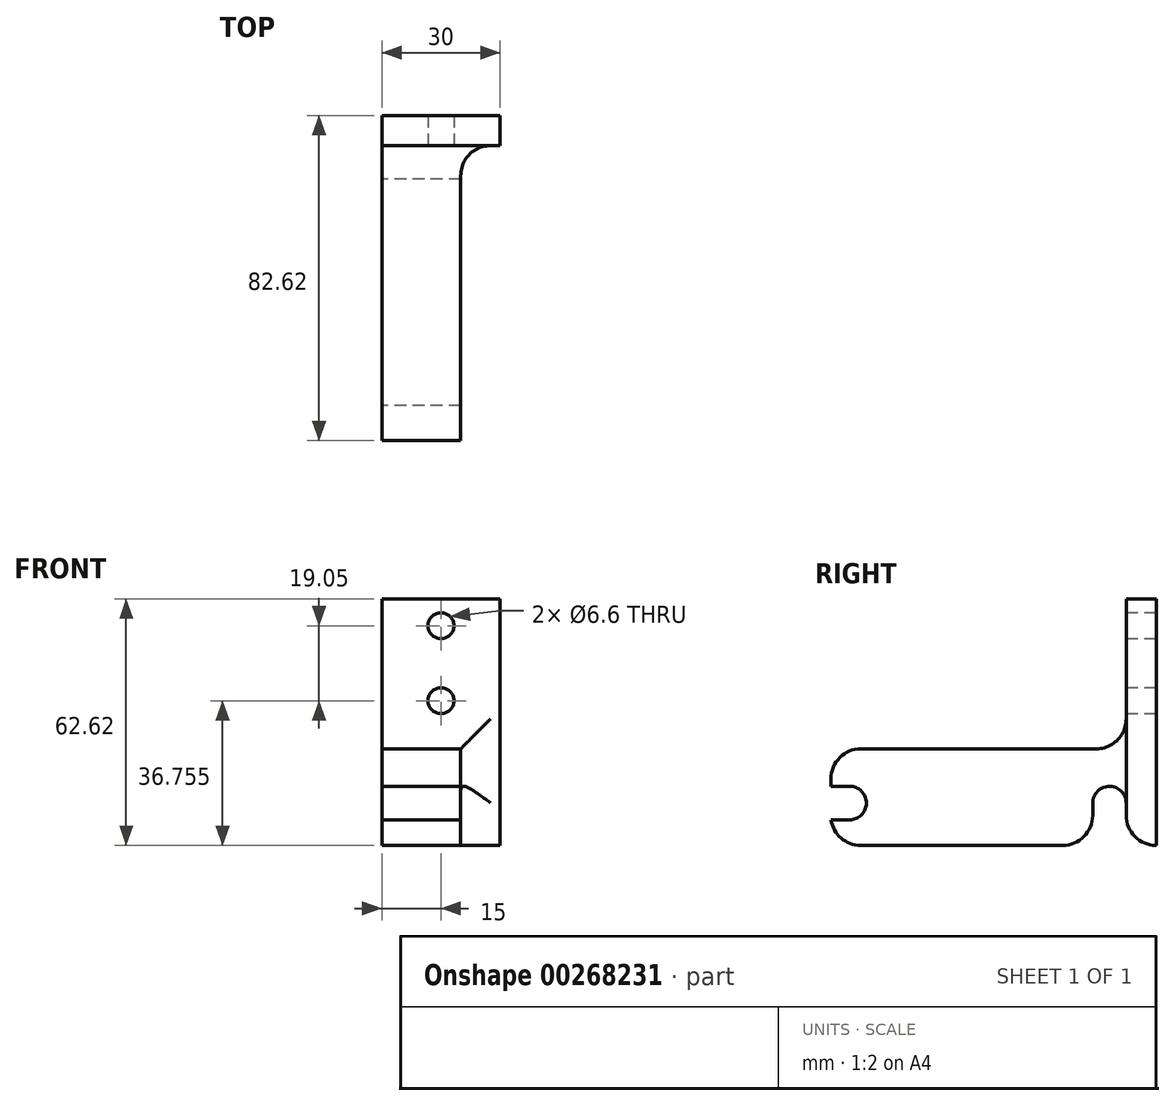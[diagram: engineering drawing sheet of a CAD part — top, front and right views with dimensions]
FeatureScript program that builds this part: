
annotation { "Feature Type Name" : "Feature", "Feature Type Description" : "" }
export const myFeature = defineFeature(function(context is Context, id is Id, definition is map)
    precondition{}
    {
        {
            var Q0;
            Q0=qCreatedBy(makeId("Right.planeOp"),FACE);
            var sketch = newSketch(context, id + "F0", { "sketchPlane" : qUnion([Q0])});
            skLineSegment(sketch, "E0", {"start": v(0, 0) * mm, "end": v(0, 6.5) * mm});
            skLineSegment(sketch, "E1", {"start": v(0, 6.5) * mm, "end": v(4.75, 6.5) * mm});
            skLineSegment(sketch, "E2", {"start": v(4.75, 15) * mm, "end": v(0, 15) * mm});
            skLineSegment(sketch, "E3", {"start": v(0, 15) * mm, "end": v(0, 16.9) * mm});
            skLineSegment(sketch, "E4", {"start": v(7.62, 24.53) * mm, "end": v(75, 24.53) * mm});
            skLineSegment(sketch, "E5", {"start": v(75, 24.53) * mm, "end": v(75, 62.63) * mm});
            skLineSegment(sketch, "E6", {"start": v(75, 62.63) * mm, "end": v(82.62, 62.63) * mm});
            skLineSegment(sketch, "E7", {"start": v(82.62, 62.63) * mm, "end": v(82.62, 0) * mm});
            skLineSegment(sketch, "E8", {"start": v(82.62, 0) * mm, "end": v(75, 0) * mm});
            skLineSegment(sketch, "E9", {"start": v(75, 0) * mm, "end": v(75, 10.75) * mm});
            skLineSegment(sketch, "E10", {"start": v(66.5, 10.75) * mm, "end": v(66.5, 0) * mm});
            skArc(sketch, "E11", {"start": v(4.75, 6.5) * mm, "mid": v(9, 10.75) * mm, "end": v(4.75, 15) * mm});
            skPoint(sketch, "E11.first.point", {"position": v(9, 10.75) * mm});
            skPoint(sketch, "E11.second.point", {"position": v(4.75, 15) * mm});
            skPoint(sketch, "E11.third.point", {"position": v(4.75, 6.5) * mm});
            skArc(sketch, "E12", {"start": v(75, 10.75) * mm, "mid": v(70.75, 15) * mm, "end": v(66.5, 10.75) * mm});
            skPoint(sketch, "E12.first.point", {"position": v(70.75, 15) * mm});
            skPoint(sketch, "E12.second.point", {"position": v(66.5, 10.75) * mm});
            skPoint(sketch, "E12.third.point", {"position": v(75, 10.75) * mm});
            skPoint(sketch, "E13.orphan", {"position": v(9, 15) * mm});
            skPoint(sketch, "E14.orphan", {"position": v(9, 6.5) * mm});
            skPoint(sketch, "E15.orphan", {"position": v(66.5, 15) * mm});
            skPoint(sketch, "E16.orphan", {"position": v(75, 15) * mm});
            skLineSegment(sketch, "E17", {"start": v(0, 0) * mm, "end": v(66.5, 0) * mm});
            skPoint(sketch, "E18.visualSharp", {"position": v(0, 24.53) * mm});
            skArc(sketch, "E18.filletArc", {"start": v(7.62, 24.53) * mm, "mid": v(2.23, 22.3) * mm, "end": v(0, 16.9) * mm});
            skSolve(sketch);
        }
        {
            var Q0;
            Q0=makeQuery(id+"F0.imprint","IMPRINT",FACE,{"disambiguationData":[TD([[makeQuery(id+"F0.imprint","IMPRINT",EDGE,{"derivedFrom":sQuery(id+"F0.wireOp",EDGE,"E0")}),-1.0]])]});
            extrude(context, id + "F1", {"entities" : qUnion([Q0]), "depth" : 30 * mm});
        }
        {
            var Q0;
            Q0=makeQuery(id+"F1.opExtrude","SWEPT_FACE",FACE,{"disambiguationData":[OSD([sQuery(id+"F0.wireOp",EDGE,"E4")])]});
            var sketch = newSketch(context, id + "F2", { "sketchPlane" : qUnion([Q0])});
            skLineSegment(sketch, "E19.bottom", {"start": v(30, 75) * mm, "end": v(20, 75) * mm});
            skLineSegment(sketch, "E19.top", {"start": v(30, 0) * mm, "end": v(20, 0) * mm});
            skLineSegment(sketch, "E19.left", {"start": v(30, 75) * mm, "end": v(30, 0) * mm});
            skLineSegment(sketch, "E19.right", {"start": v(20, 75) * mm, "end": v(20, 0) * mm});
            skPoint(sketch, "E20.0", {"position": v(30, 0) * mm});
            skSolve(sketch);
        }
        {
            var Q0;
            Q0=makeQuery(id+"F2.imprint","IMPRINT",FACE,{"disambiguationData":[TD([[makeQuery(id+"F2.imprint","IMPRINT",EDGE,{"derivedFrom":sQuery(id+"F2.wireOp",EDGE,"E19.bottom")}),1.0]])]});
            var Q1;
            {var subQ0=sQuery(id+"F2.wireOp",EDGE,"E19.top");Q1=makeQuery(id+"F2.imprint","IMPRINT",FACE,{"disambiguationData":[TD([[makeQuery(id+"F2.imprint","IMPRINT",EDGE,{"derivedFrom":subQ0}),-1.0]])]});}
            var Q2;
            Q2=makeQuery(id+"F1.opExtrude","SWEPT_BODY",BODY,{"disambiguationData":[OSD([sQuery(id+"F0.wireOp",EDGE,"E0"),sQuery(id+"F0.wireOp",EDGE,"E1"),sQuery(id+"F0.wireOp",EDGE,"E2"),sQuery(id+"F0.wireOp",EDGE,"E3"),sQuery(id+"F0.wireOp",EDGE,"E4"),sQuery(id+"F0.wireOp",EDGE,"E5"),sQuery(id+"F0.wireOp",EDGE,"E6"),sQuery(id+"F0.wireOp",EDGE,"E7"),sQuery(id+"F0.wireOp",EDGE,"E8"),sQuery(id+"F0.wireOp",EDGE,"E9"),sQuery(id+"F0.wireOp",EDGE,"E10"),sQuery(id+"F0.wireOp",EDGE,"E11"),sQuery(id+"F0.wireOp",EDGE,"E12"),sQuery(id+"F0.wireOp",EDGE,"E17")])]});
            extrude(context, id + "F3", {"entities" : qUnion([Q0, Q1]), "operationType" : NewBodyOperationType.REMOVE, "endBound" : BoundingType.UP_TO_BODY, "oppositeDirection" : true, "endBoundEntityBody" : qUnion([Q2]), "depth" : 25.4 * mm});
        }
        {
            var Q0;
            Q0=makeQuery(id+"F1.opExtrude","SWEPT_EDGE",EDGE,{"disambiguationData":[OSD([sQuery(id+"F0.wireOp",EDGE,"E3"),sQuery(id+"F0.wireOp",EDGE,"E18.filletArc")])]});
            var Q1;
            Q1=makeQuery(id+"F1.opExtrude","SWEPT_EDGE",EDGE,{"disambiguationData":[OSD([sQuery(id+"F0.wireOp",EDGE,"E4"),sQuery(id+"F0.wireOp",EDGE,"E18.filletArc")])]});
            var Q2;
            Q2=makeQuery(id+"F1.opExtrude","SWEPT_EDGE",EDGE,{"disambiguationData":[OSD([sQuery(id+"F0.wireOp",EDGE,"E4"),sQuery(id+"F0.wireOp",EDGE,"E5")])]});
            var Q3;
            Q3=makeQuery(id+"F1.opExtrude","SWEPT_EDGE",EDGE,{"disambiguationData":[OSD([sQuery(id+"F0.wireOp",EDGE,"E4"),sQuery(id+"F0.wireOp",EDGE,"E5")])]});
            var Q4;
            Q4=makeQuery(id+"F3.boolean.opBoolean","COPY",EDGE,{"derivedFrom":makeQuery(id+"F3.opExtrude","SWEPT_EDGE",EDGE,{"disambiguationData":[OSD([sQuery(id+"F0.wireOp",EDGE,"E4"),sQuery(id+"F0.wireOp",EDGE,"E5"),sQuery(id+"F2.wireOp",EDGE,"E19.bottom"),sQuery(id+"F2.wireOp",EDGE,"E19.right")])]})});
            var Q5;
            Q5=makeQuery(id+"F3.boolean.opBoolean","COPY",EDGE,{"derivedFrom":makeQuery(id+"F3.opExtrude","CAP_EDGE",EDGE,{"disambiguationData":[OSD([sQuery(id+"F2.wireOp",EDGE,"E19.right")])],"isStart":true})});
            var Q6;
            Q6=makeQuery(id+"F1.opExtrude","SWEPT_EDGE",EDGE,{"disambiguationData":[OSD([sQuery(id+"F0.wireOp",EDGE,"E10"),sQuery(id+"F0.wireOp",EDGE,"E17")])]});
            var Q7;
            Q7=makeQuery(id+"F1.opExtrude","SWEPT_EDGE",EDGE,{"disambiguationData":[OSD([sQuery(id+"F0.wireOp",EDGE,"E8"),sQuery(id+"F0.wireOp",EDGE,"E9")])]});
            var Q8;
            Q8=makeQuery(id+"F1.opExtrude","SWEPT_EDGE",EDGE,{"disambiguationData":[OSD([sQuery(id+"F0.wireOp",EDGE,"E0"),sQuery(id+"F0.wireOp",EDGE,"E17")])]});
            fillet(context, id + "F4", {"entities" : qUnion([Q0, Q1, Q2, Q3, Q4, Q5, Q6, Q7, Q8]), "radius" : 7.62 * mm, "allowEdgeOverflow" : false});
        }
        {
            var Q0;
            Q0=makeQuery(id+"F3.boolean.opBoolean","MERGE",FACE,{"derivedFrom":[makeQuery(id+"F1.opExtrude","SWEPT_FACE",FACE,{"disambiguationData":[OSD([sQuery(id+"F0.wireOp",EDGE,"E5")])]}),makeQuery(id+"F1.opExtrude","SWEPT_FACE",FACE,{"disambiguationData":[OSD([sQuery(id+"F0.wireOp",EDGE,"E9")])]}),makeQuery(id+"F3.opExtrude","SWEPT_FACE",FACE,{"disambiguationData":[OSD([sQuery(id+"F2.wireOp",EDGE,"E19.bottom")])]})]});
            var sketch = newSketch(context, id + "F5", { "sketchPlane" : qUnion([Q0])});
            skPoint(sketch, "E21.0", {"position": v(15, 62.63) * mm});
            skPoint(sketch, "E22", {"position": v(15, 55.8) * mm});
            skPoint(sketch, "E23", {"position": v(15, 36.76) * mm});
            skSolve(sketch);
        }
        {
            var Q0;
            Q0=sQuery(id+"F5.wireOp",VERTEX,"E22");
            var Q1;
            Q1=sQuery(id+"F5.wireOp",VERTEX,"E23");
            var Q2;
            Q2=makeQuery(id+"F1.opExtrude","SWEPT_BODY",BODY,{"disambiguationData":[OSD([sQuery(id+"F0.wireOp",EDGE,"E0"),sQuery(id+"F0.wireOp",EDGE,"E1"),sQuery(id+"F0.wireOp",EDGE,"E2"),sQuery(id+"F0.wireOp",EDGE,"E3"),sQuery(id+"F0.wireOp",EDGE,"E4"),sQuery(id+"F0.wireOp",EDGE,"E5"),sQuery(id+"F0.wireOp",EDGE,"E6"),sQuery(id+"F0.wireOp",EDGE,"E7"),sQuery(id+"F0.wireOp",EDGE,"E8"),sQuery(id+"F0.wireOp",EDGE,"E9"),sQuery(id+"F0.wireOp",EDGE,"E10"),sQuery(id+"F0.wireOp",EDGE,"E11"),sQuery(id+"F0.wireOp",EDGE,"E12"),sQuery(id+"F0.wireOp",EDGE,"E17"),sQuery(id+"F0.wireOp",EDGE,"E18.filletArc")])]});
            hole(context, id + "F6", {"style" : HoleStyle.SIMPLE, "endStyle" : HoleEndStyle.THROUGH, "standardTappedOrClearance" : lookupTablePath({ "standard" : "ISO", "fit" : "Normal", "size" : "M6", "type" : "Clearance" }), "standardBlindInLast" : lookupTablePath({ "fit" : "Standard", "standard" : "ISO", "size" : "M6", "type" : "Clearance" }), "holeDiameter" : 6.6 * mm, "tappedDepth" : 12.7 * mm, "tapClearance" : 3, "locations" : qUnion([Q0, Q1]), "scope" : qUnion([Q2])});
        }
    });
